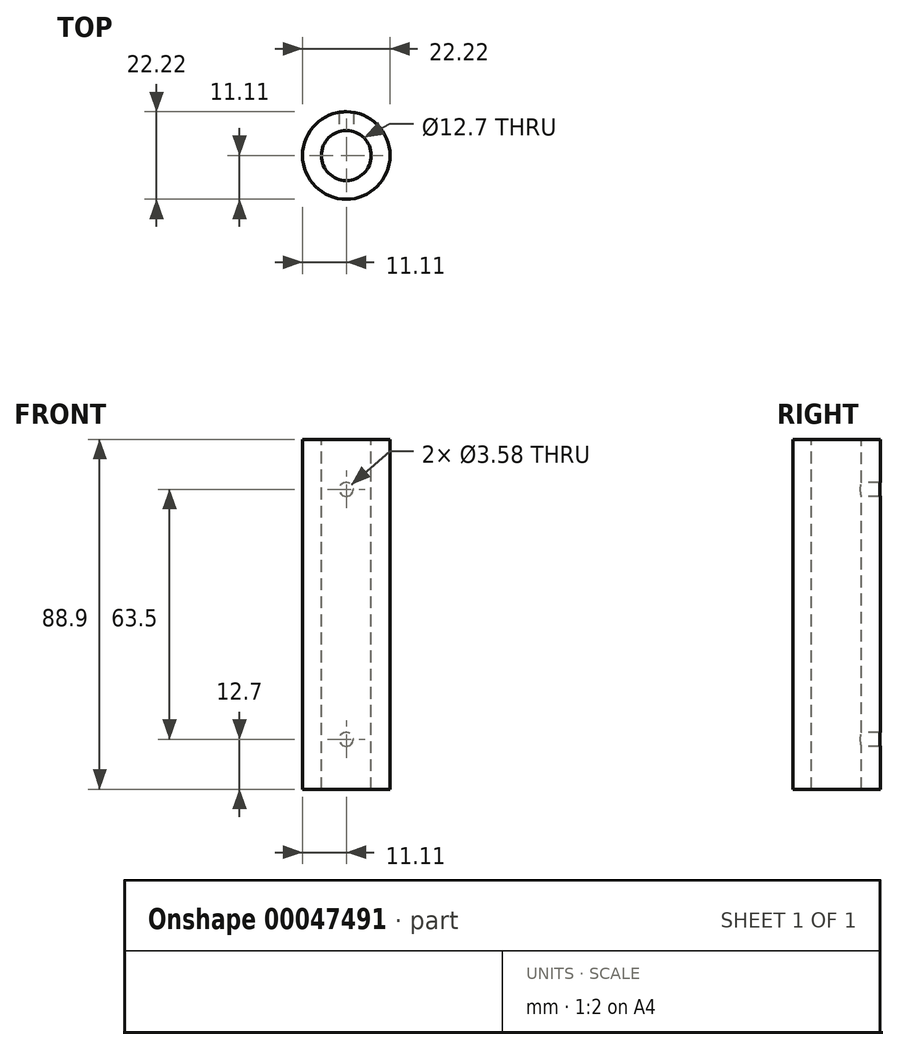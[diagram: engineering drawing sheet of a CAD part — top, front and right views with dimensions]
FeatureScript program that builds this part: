
annotation { "Feature Type Name" : "Feature", "Feature Type Description" : "" }
export const myFeature = defineFeature(function(context is Context, id is Id, definition is map)
    precondition{}
    {
        {
            var Q0;
            Q0=qCreatedBy(makeId("Top.planeOp"),FACE);
            var sketch = newSketch(context, id + "F0", { "sketchPlane" : qUnion([Q0])});
            skCircle(sketch, "E0", {"center": v(0, 0) * mm, "radius": 11.11 * mm});
            skSolve(sketch);
        }
        {
            var Q0;
            Q0 = qSketchRegion(id + "F0", true);
            extrude(context, id + "F1", {"entities" : qUnion([Q0]), "depth" : 88.9 * mm, "symmetric" : true});
        }
        {
            var Q0;
            Q0=makeQuery(id+"F1.opExtrude","CAP_FACE",FACE,{"disambiguationData":[OSD([sQuery(id+"F0.wireOp",EDGE,"E0")])],"isStart":false});
            var sketch = newSketch(context, id + "F2", { "sketchPlane" : qUnion([Q0])});
            skCircle(sketch, "E1", {"center": v(0, 0) * mm, "radius": 6.35 * mm});
            skSolve(sketch);
        }
        {
            var Q0;
            Q0 = qSketchRegion(id + "F2", true);
            extrude(context, id + "F3", {"entities" : qUnion([Q0]), "operationType" : NewBodyOperationType.REMOVE, "endBound" : BoundingType.THROUGH_ALL, "oppositeDirection" : true, "depth" : 25.4 * mm});
        }
        {
            var Q0;
            Q0=qCreatedBy(makeId("Front.planeOp"),FACE);
            var sketch = newSketch(context, id + "F4", { "sketchPlane" : qUnion([Q0])});
            skCircle(sketch, "E2", {"center": v(0, 31.75) * mm, "radius": 1.8 * mm});
            skCircle(sketch, "E3.MirrorC", {"center": v(0, -31.75) * mm, "radius": 1.8 * mm});
            skSolve(sketch);
        }
        {
            var Q0;
            Q0 = qSketchRegion(id + "F4", true);
            var Q1;
            Q1=makeQuery(id+"F1.opExtrude","SWEPT_FACE",FACE,{"disambiguationData":[OSD([sQuery(id+"F0.wireOp",EDGE,"E0")])]});
            extrude(context, id + "F5", {"entities" : qUnion([Q0]), "operationType" : NewBodyOperationType.REMOVE, "oppositeDirection" : true, "endBoundEntityFace" : qUnion([Q1]), "depth" : 25.4 * mm});
        }
    });
